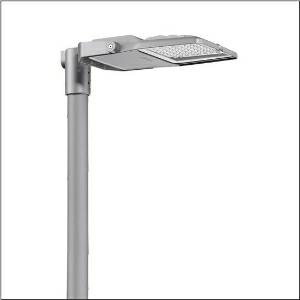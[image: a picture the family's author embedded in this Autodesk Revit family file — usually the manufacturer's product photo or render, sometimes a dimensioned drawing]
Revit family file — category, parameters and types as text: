
# Revit family: floodlight_fl_21_mini___pl52_5xa7775b2d3a_6ba7
name_source: partatom
category: Lighting Fixtures
units: mm (PartAtom-declared; Revit-internal decimal feet)

## family parameters
Cut with Voids When Loaded = No
Host = Face
Light Source = No
Part Type = Normal
Room Calculation Point = No
Round Connector Dimension = Use Diameter
Shared = No

## types (1)
- --- (1 x LED, 6230 lm, 45.7 W, 3000K)
    Apparent Load = 46 VA
    CIE Flux Codes = 26 60 98 100 100
    Color Rendering = 70
    Color Temperature = 3000K
    Default Elevation = 1800 mm
    Description = Floodlight FL 21 mini, floodlight, primary light control with lens, of PMMA, primary optical cover: protective disc, of toughened safety glass, transparent, light distribution: PL52, light emission: direct distribution, installation type: surface-mounted, LED, High Power LED, rated luminous flux: 6.230lm, luminous efficacy: 136lm/W, light colour: 730, colour temperature: 3000K, control gear: Smart Interface (Zhaga), control: flexible luminous flux parameterisation, time-dependent luminous flux control, constant luminous flux control, overheat protection, pre-setting: logarithmic dimming characteristic, with terminal, 6-pole, mains connection: 220..240V, AC, 50/60Hz, start of lifetime: 46W, end of service life: 48W, reduction: 22W, luminaire housing, of diecast aluminium, powder-coated, Siteco® metallic grey (DB 702S), corrosivity category C5 mid according to DIN EN ISO 12944, suitable for swimming pools, chlorine-resistant, sealing non-destructively replaceable, please order mast flange separately, mast bracket, of steel, galvanised, powder-coated, Siteco® metallic grey (DB 702S), Smart Interface above, protection rating (complete): IP66, insulation class (complete): insulation class II (safety insulation), certification: CE, ENEC, VDE, protection symbol: D, impact resistance: IK08, permissible operating ambient temperature: -40..+40°C, permissible operating ambient temperature for outdoor applications: -40..+50°C, standard: DIN EN 12944, LABS conformity tested according to VDMA 24364:2018-05, packaging unit: 1 piece

Light Distribution: PL52
    Height = 70 mm
    Lamp = 1 x LED
    Lamp Light Flux = 6230 lm
    Lamp Power = 45.7 W
    Lamp count = 1
    Length = 485 mm
    Luminous efficacy = 136 lm/W
    Manufacturer = Siteco
    ModVariant = No
    Model = 5XA7775B2D3A
    Number of Poles = 1
    OnlyDefault = Yes
    Power Factor = 1
    Product Name = Floodlight FL 21 mini | PL52
    Product group = floodlight | pylon annexe
    ProductGroupID = 6200
    Protection Class = Protection class II
    Protection Degree = IP 66
    RLX_Detail_Level = 1
    RLX_Emergency_Light_Flux = 0 lm
    RLX_Emergency_Type = 0
    RLX_Emergency_Type_DB = No
    RlxData = <blob elided: 101161 chars, md5=c0cb8f0a>
    Socket = socket
    Standby Power = 0 W
    System Light Flux = 6230 lm
    System Power = 46 W
    Type Comments = factory setting: luminous flux: 100 % | dim-lin: 254 | 463 mA
    Type Image = l_1007125.jpg
    URL = http://relux.com
    VarID = @adj_163454
    Voltage = 0 V
    Weight = 0.00 kg
    Width = 337 mm

## geometry (parser evidence)
native form markers: Blend x4, Sweep x13
no freeform markers — native parametric forms only
